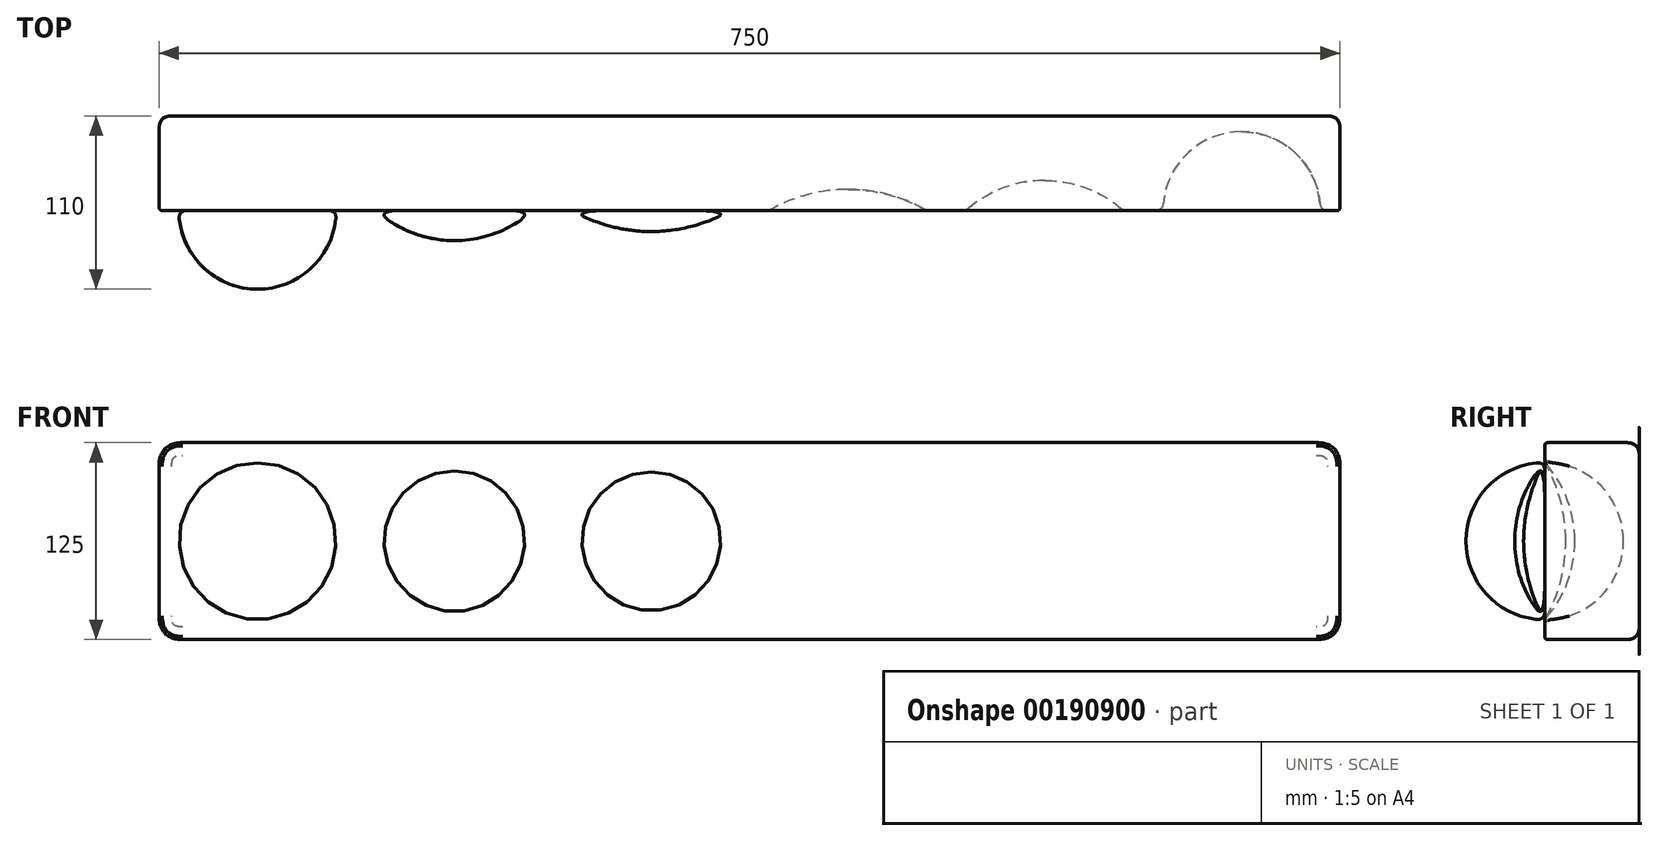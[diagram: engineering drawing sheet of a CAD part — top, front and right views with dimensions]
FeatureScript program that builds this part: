
annotation { "Feature Type Name" : "Feature", "Feature Type Description" : "" }
export const myFeature = defineFeature(function(context is Context, id is Id, definition is map)
    precondition{}
    {
        {
            var Q0;
            Q0=qCreatedBy(makeId("Front.planeOp"),FACE);
            var sketch = newSketch(context, id + "F0", { "sketchPlane" : qUnion([Q0])});
            skLineSegment(sketch, "E0.bottom", {"start": v(375, 62.5) * mm, "end": v(-375, 62.5) * mm});
            skLineSegment(sketch, "E0.top", {"start": v(375, -62.5) * mm, "end": v(-375, -62.5) * mm});
            skLineSegment(sketch, "E0.left", {"start": v(375, 62.5) * mm, "end": v(375, -62.5) * mm});
            skLineSegment(sketch, "E0.right", {"start": v(-375, 62.5) * mm, "end": v(-375, -62.5) * mm});
            skPoint(sketch, "E0.middle", {"position": v(0, 0) * mm});
            skCircle(sketch, "E1", {"center": v(-312.5, 0) * mm, "radius": 50 * mm});
            skCircle(sketch, "E2.1.0.0", {"center": v(-187.5, 0) * mm, "radius": 50 * mm});
            skCircle(sketch, "E2.2.0.0", {"center": v(-62.5, 0) * mm, "radius": 50 * mm});
            skCircle(sketch, "E2.3.0.0", {"center": v(62.5, 0) * mm, "radius": 50 * mm});
            skCircle(sketch, "E2.4.0.0", {"center": v(187.5, 0) * mm, "radius": 50 * mm});
            skCircle(sketch, "E2.5.0.0", {"center": v(312.5, 0) * mm, "radius": 50 * mm});
            skLineSegment(sketch, "E2.direction1", {"start": v(-312.5, 0) * mm, "end": v(-187.5, 0) * mm, "construction": true});
            skCircle(sketch, "E3", {"center": v(-312.5, 0) * mm, "radius": 62.5 * mm, "construction": true});
            skPoint(sketch, "E4", {"position": v(-250, 0) * mm});
            skSolve(sketch);
        }
        {
            var Q0;
            Q0=qCreatedBy(makeId("Front.planeOp"),FACE);
            var sketch = newSketch(context, id + "F1", { "sketchPlane" : qUnion([Q0])});
            skLineSegment(sketch, "E5.0", {"start": v(-375, 62.5) * mm, "end": v(-375, -62.5) * mm});
            skLineSegment(sketch, "E5.1", {"start": v(375, 62.5) * mm, "end": v(-375, 62.5) * mm});
            skLineSegment(sketch, "E5.2", {"start": v(375, 62.5) * mm, "end": v(375, -62.5) * mm});
            skLineSegment(sketch, "E5.3", {"start": v(375, -62.5) * mm, "end": v(-375, -62.5) * mm});
            skSolve(sketch);
        }
        {
            var Q0;
            Q0 = qSketchRegion(id + "F1", true);
            extrude(context, id + "F2", {"entities" : qUnion([Q0]), "oppositeDirection" : true, "depth" : 60 * mm, "offsetDistance" : 25 * mm});
        }
        {
            var Q0;
            Q0=qCreatedBy(makeId("Top.planeOp"),FACE);
            var sketch = newSketch(context, id + "F3", { "sketchPlane" : qUnion([Q0])});
            skArc(sketch, "E6", {"start": v(-362.5, 0) * mm, "mid": v(-347.86, -35.36) * mm, "end": v(-312.5, -50) * mm});
            skLineSegment(sketch, "E7", {"start": v(-362.5, 0) * mm, "end": v(-312.5, 0) * mm});
            skLineSegment(sketch, "E8", {"start": v(-312.5, 0) * mm, "end": v(-312.5, -50) * mm});
            skSolve(sketch);
        }
        {
            var Q0;
            Q0 = qSketchRegion(id + "F3", true);
            var Q1;
            Q1=sQuery(id+"F3.wireOp",EDGE,"E8");
            revolve(context, id + "F4", {"surfaceOperationType" : NewSurfaceOperationType.NEW, "entities" : qUnion([Q0]), "axis" : qUnion([Q1]), "revolveType" : RevolveType.FULL});
        }
        {
            var Q0;
            Q0=qCreatedBy(makeId("Top.planeOp"),FACE);
            var sketch = newSketch(context, id + "F5", { "sketchPlane" : qUnion([Q0])});
            skArc(sketch, "E9", {"start": v(-237.5, 0) * mm, "mid": v(-214.26, -14.16) * mm, "end": v(-187.5, -19.1) * mm});
            skLineSegment(sketch, "E10", {"start": v(-237.5, 0) * mm, "end": v(-187.5, 0) * mm});
            skLineSegment(sketch, "E11", {"start": v(-187.5, 0) * mm, "end": v(-187.5, -19.1) * mm});
            skSolve(sketch);
        }
        {
            var Q0;
            Q0 = qSketchRegion(id + "F5", true);
            var Q1;
            Q1=sQuery(id+"F5.wireOp",EDGE,"E11");
            revolve(context, id + "F6", {"surfaceOperationType" : NewSurfaceOperationType.NEW, "entities" : qUnion([Q0]), "axis" : qUnion([Q1]), "revolveType" : RevolveType.FULL});
        }
        {
            var Q0;
            Q0=qCreatedBy(makeId("Top.planeOp"),FACE);
            var sketch = newSketch(context, id + "F7", { "sketchPlane" : qUnion([Q0])});
            skArc(sketch, "E12", {"start": v(-112.5, 0) * mm, "mid": v(-88.38, -10) * mm, "end": v(-62.5, -13.4) * mm});
            skLineSegment(sketch, "E13", {"start": v(-112.5, 0) * mm, "end": v(-62.5, 0) * mm});
            skLineSegment(sketch, "E14", {"start": v(-62.5, 0) * mm, "end": v(-62.5, -13.4) * mm});
            skSolve(sketch);
        }
        {
            var Q0;
            Q0 = qSketchRegion(id + "F7", true);
            var Q1;
            Q1=sQuery(id+"F7.wireOp",EDGE,"E14");
            revolve(context, id + "F8", {"surfaceOperationType" : NewSurfaceOperationType.NEW, "entities" : qUnion([Q0]), "axis" : qUnion([Q1]), "revolveType" : RevolveType.FULL});
        }
        {
            var Q0;
            Q0=qCreatedBy(makeId("Front.planeOp"),FACE);
            var sketch = newSketch(context, id + "F9", { "sketchPlane" : qUnion([Q0])});
            skLineSegment(sketch, "E15", {"start": v(0, -127.8) * mm, "end": v(0, 135.47) * mm, "construction": true});
            skSolve(sketch);
        }
        {
            var Q0;
            Q0=makeQuery(id+"F8.opRevolve","SWEPT_BODY",BODY,{"disambiguationData":[OSD([sQuery(id+"F7.wireOp",EDGE,"E12"),sQuery(id+"F7.wireOp",EDGE,"E13"),sQuery(id+"F7.wireOp",EDGE,"E14")])]});
            var Q1;
            Q1=makeQuery(id+"F6.opRevolve","SWEPT_BODY",BODY,{"disambiguationData":[OSD([sQuery(id+"F5.wireOp",EDGE,"E9"),sQuery(id+"F5.wireOp",EDGE,"E10"),sQuery(id+"F5.wireOp",EDGE,"E11")])]});
            var Q2;
            Q2=makeQuery(id+"F4.opRevolve","SWEPT_BODY",BODY,{"disambiguationData":[OSD([sQuery(id+"F3.wireOp",EDGE,"E6"),sQuery(id+"F3.wireOp",EDGE,"E7"),sQuery(id+"F3.wireOp",EDGE,"E8")])]});
            var Q3;
            Q3=sQuery(id+"F9.wireOp",EDGE,"E15");
            circularPattern(context, id + "F10", {"entities" : qUnion([Q0, Q1, Q2]), "axis" : qUnion([Q3]), "angle" : 180 * degree, "instanceCount" : 2, "equalSpace" : true});
        }
        {
            var Q0;
            Q0=makeQuery(id+"F10.opPattern","COPY",BODY,{"derivedFrom":makeQuery(id+"F8.opRevolve","SWEPT_BODY",BODY,{"disambiguationData":[OSD([sQuery(id+"F7.wireOp",EDGE,"E12"),sQuery(id+"F7.wireOp",EDGE,"E13"),sQuery(id+"F7.wireOp",EDGE,"E14")])]}),"instanceName":"1"});
            var Q1;
            Q1=makeQuery(id+"F10.opPattern","COPY",BODY,{"derivedFrom":makeQuery(id+"F6.opRevolve","SWEPT_BODY",BODY,{"disambiguationData":[OSD([sQuery(id+"F5.wireOp",EDGE,"E9"),sQuery(id+"F5.wireOp",EDGE,"E10"),sQuery(id+"F5.wireOp",EDGE,"E11")])]}),"instanceName":"1"});
            var Q2;
            Q2=makeQuery(id+"F10.opPattern","COPY",BODY,{"derivedFrom":makeQuery(id+"F4.opRevolve","SWEPT_BODY",BODY,{"disambiguationData":[OSD([sQuery(id+"F3.wireOp",EDGE,"E6"),sQuery(id+"F3.wireOp",EDGE,"E7"),sQuery(id+"F3.wireOp",EDGE,"E8")])]}),"instanceName":"1"});
            var Q3;
            Q3=makeQuery(id+"F2.opExtrude","SWEPT_BODY",BODY,{"disambiguationData":[OSD([sQuery(id+"F1.wireOp",EDGE,"E5.0"),sQuery(id+"F1.wireOp",EDGE,"E5.1"),sQuery(id+"F1.wireOp",EDGE,"E5.2"),sQuery(id+"F1.wireOp",EDGE,"E5.3")])]});
            booleanBodies(context, id + "F11", {"operationType" : BooleanOperationType.SUBTRACTION, "tools" : qUnion([Q0, Q1, Q2]), "targets" : qUnion([Q3])});
        }
        {
            var Q0;
            Q0=makeQuery(id+"F2.opExtrude","SWEPT_EDGE",EDGE,{"disambiguationData":[OSD([sQuery(id+"F1.wireOp",EDGE,"E5.0"),sQuery(id+"F1.wireOp",EDGE,"E5.1")])]});
            var Q1;
            Q1=makeQuery(id+"F2.opExtrude","SWEPT_EDGE",EDGE,{"disambiguationData":[OSD([sQuery(id+"F1.wireOp",EDGE,"E5.0"),sQuery(id+"F1.wireOp",EDGE,"E5.3")])]});
            var Q2;
            Q2=makeQuery(id+"F2.opExtrude","SWEPT_EDGE",EDGE,{"disambiguationData":[OSD([sQuery(id+"F1.wireOp",EDGE,"E5.1"),sQuery(id+"F1.wireOp",EDGE,"E5.2")])]});
            var Q3;
            Q3=makeQuery(id+"F2.opExtrude","SWEPT_EDGE",EDGE,{"disambiguationData":[OSD([sQuery(id+"F1.wireOp",EDGE,"E5.2"),sQuery(id+"F1.wireOp",EDGE,"E5.3")])]});
            fillet(context, id + "F12", {"entities" : qUnion([Q0, Q1, Q2, Q3]), "tangentPropagation" : true, "crossSection" : FilletCrossSection.CURVATURE, "radius" : 15 * mm, "magnitude" : 0.5, "defaultsChanged" : true, "vertexSettings" : []});
        }
        {
            var Q0;
            Q0=makeQuery(id+"F2.opExtrude","CAP_EDGE",EDGE,{"disambiguationData":[OSD([sQuery(id+"F1.wireOp",EDGE,"E5.1")])],"isStart":false});
            fillet(context, id + "F13", {"entities" : qUnion([Q0]), "tangentPropagation" : true, "crossSection" : FilletCrossSection.CURVATURE, "radius" : 8 * mm, "magnitude" : 0.5, "defaultsChanged" : true, "vertexSettings" : []});
        }
        {
            var Q0;
            Q0=makeQuery(id+"F2.opExtrude","CAP_EDGE",EDGE,{"disambiguationData":[OSD([sQuery(id+"F1.wireOp",EDGE,"E5.1")])],"isStart":true});
            fillet(context, id + "F14", {"entities" : qUnion([Q0]), "tangentPropagation" : true, "crossSection" : FilletCrossSection.CURVATURE, "radius" : 2 * mm, "magnitude" : 0.5, "defaultsChanged" : false, "vertexSettings" : []});
        }
        {
            var Q0;
            Q0=makeQuery(id+"F4.opRevolve","SWEPT_FACE",FACE,{"disambiguationData":[OSD([sQuery(id+"F3.wireOp",EDGE,"E6")])]});
            var Q1;
            Q1=makeQuery(id+"F6.opRevolve","SWEPT_FACE",FACE,{"disambiguationData":[OSD([sQuery(id+"F5.wireOp",EDGE,"E9")])]});
            var Q2;
            Q2=makeQuery(id+"F8.opRevolve","SWEPT_FACE",FACE,{"disambiguationData":[OSD([sQuery(id+"F7.wireOp",EDGE,"E12")])]});
            var Q3;
            Q3=makeQuery(id+"F11.opBoolean","COPY",FACE,{"derivedFrom":makeQuery(id+"F10.opPattern","COPY",FACE,{"derivedFrom":makeQuery(id+"F8.opRevolve","SWEPT_FACE",FACE,{"disambiguationData":[OSD([sQuery(id+"F7.wireOp",EDGE,"E12")])]}),"instanceName":"1"})});
            var Q4;
            Q4=makeQuery(id+"F11.opBoolean","COPY",FACE,{"derivedFrom":makeQuery(id+"F10.opPattern","COPY",FACE,{"derivedFrom":makeQuery(id+"F6.opRevolve","SWEPT_FACE",FACE,{"disambiguationData":[OSD([sQuery(id+"F5.wireOp",EDGE,"E9")])]}),"instanceName":"1"})});
            var Q5;
            Q5=makeQuery(id+"F11.opBoolean","COPY",FACE,{"derivedFrom":makeQuery(id+"F10.opPattern","COPY",FACE,{"derivedFrom":makeQuery(id+"F4.opRevolve","SWEPT_FACE",FACE,{"disambiguationData":[OSD([sQuery(id+"F3.wireOp",EDGE,"E6")])]}),"instanceName":"1"})});
            fillet(context, id + "F15", {"entities" : qUnion([Q0, Q1, Q2, Q3, Q4, Q5]), "tangentPropagation" : true, "crossSection" : FilletCrossSection.CURVATURE, "radius" : 5 * mm, "magnitude" : 0.5, "defaultsChanged" : false, "vertexSettings" : []});
        }
    });
